SOLIDWORKS PART (.sldprt)
format: sldprt  version: not decoded by parser v0  size: 179,200 bytes
history: native  units: mm
features: sketch x10, plane x5, revolve x2, extrude x2, cut_extrude x2, material x1, cut_revolve x1 (+13 scaffold rows collapsed)
feature tree (36):
  scaffold x13  (default folders/planes/origin — collapsed)
  material  "材质 <未指定>"
  plane  "前视基准面"
  plane  "上视基准面"
  plane  "右视基准面"
  plane  "基准面1"  Offset=0mm
  sketch  "草图3"  dims[D1=10.0mm]
  revolve  "旋转4"  Angle=30deg
  sketch  "草图4"  dims[D1=7.0mm]
  extrude  "凸台-拉伸1"  Depth=10mm
  plane  "基准面2"
  sketch  "草图6"  dims[D1=0.0mm]
  sketch  "草图7"  dims[D1=360.0mm D2=25.0mm]
  extrude  "凸台-拉伸2"  Depth=1mm
  sketch  "草图8"
  cut_extrude  "切除-拉伸1"  [1 undecoded]
  sketch  "草图9"
  cut_extrude  "切除-拉伸2"  [1 undecoded]
  sketch  "草图10"  dims[D1=5.0mm]
  sketch  "草图11"
  sketch  "草图12"
  cut_revolve  "切除-旋转1"  Angle=360deg
  sketch  "草图13"  dims[D1=0.0mm]
  revolve  "旋转5"  Angle=360deg
decode coverage: 11 of 17 modeling features carry decoded parameters
note: 2 parameter values undecoded
note: suppression state not decoded; provenance and decode notes live in map.json
